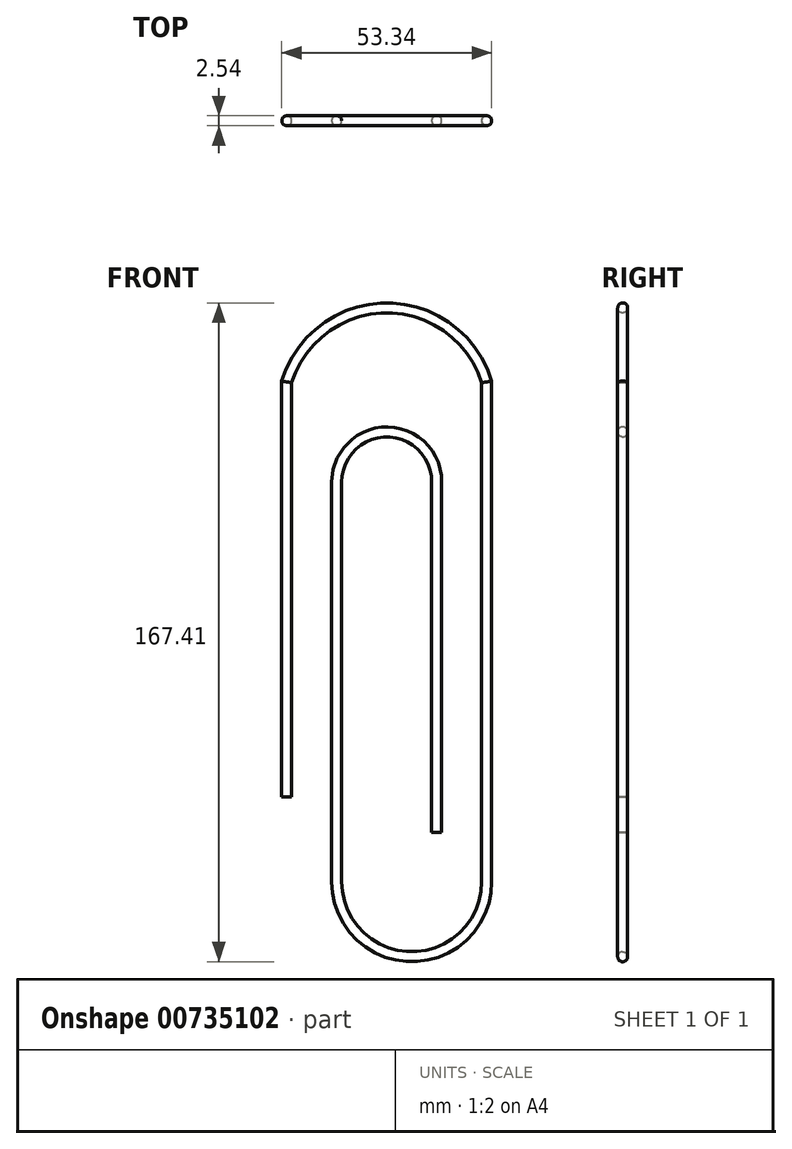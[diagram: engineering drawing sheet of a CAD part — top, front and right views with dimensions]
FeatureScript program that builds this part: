
annotation { "Feature Type Name" : "Feature", "Feature Type Description" : "" }
export const myFeature = defineFeature(function(context is Context, id is Id, definition is map)
    precondition{}
    {
        {
            var Q0;
            Q0=qCreatedBy(makeId("Front.planeOp"),FACE);
            var sketch = newSketch(context, id + "F0", { "sketchPlane" : qUnion([Q0])});
            skLineSegment(sketch, "E0", {"start": v(0, 105.41) * mm, "end": v(0, 0) * mm});
            skLineSegment(sketch, "E1", {"start": v(12.7, 80.01) * mm, "end": v(12.7, -21.59) * mm});
            skLineSegment(sketch, "E2", {"start": v(38.1, 80.01) * mm, "end": v(38.1, -9) * mm});
            skLineSegment(sketch, "E3", {"start": v(50.8, 105.41) * mm, "end": v(50.8, -21.59) * mm});
            skArc(sketch, "E4", {"start": v(50.8, 105.41) * mm, "mid": v(25.4, 124.23) * mm, "end": v(0, 105.41) * mm});
            skArc(sketch, "E5", {"start": v(38.1, 80.01) * mm, "mid": v(25.4, 92.71) * mm, "end": v(12.7, 80.01) * mm});
            skArc(sketch, "E6", {"start": v(12.7, -21.59) * mm, "mid": v(31.75, -40.64) * mm, "end": v(50.8, -21.59) * mm});
            skLineSegment(sketch, "E7", {"start": v(77.82, -21.59) * mm, "end": v(-31.4, -21.59) * mm, "construction": true});
            skLineSegment(sketch, "E8", {"start": v(63, 105.41) * mm, "end": v(-111.13, 105.41) * mm, "construction": true});
            skSolve(sketch);
        }
        {
            var Q0;
            Q0=qCreatedBy(makeId("Top.planeOp"),FACE);
            var sketch = newSketch(context, id + "F1", { "sketchPlane" : qUnion([Q0])});
            skCircle(sketch, "E9", {"center": v(0, 0) * mm, "radius": 1.27 * mm});
            skSolve(sketch);
        }
        {
            var Q0;
            Q0=qSketchRegion(id+"F1",true);
            var Q1;
            Q1=qConstructionFilter(qBodyType(qCreatedBy(id+"F0",EDGE),BodyType.WIRE),ConstructionObject.NO);
            sweep(context, id + "F2", {"profiles" : qUnion([Q0]), "path" : qUnion([Q1])});
        }
    });
